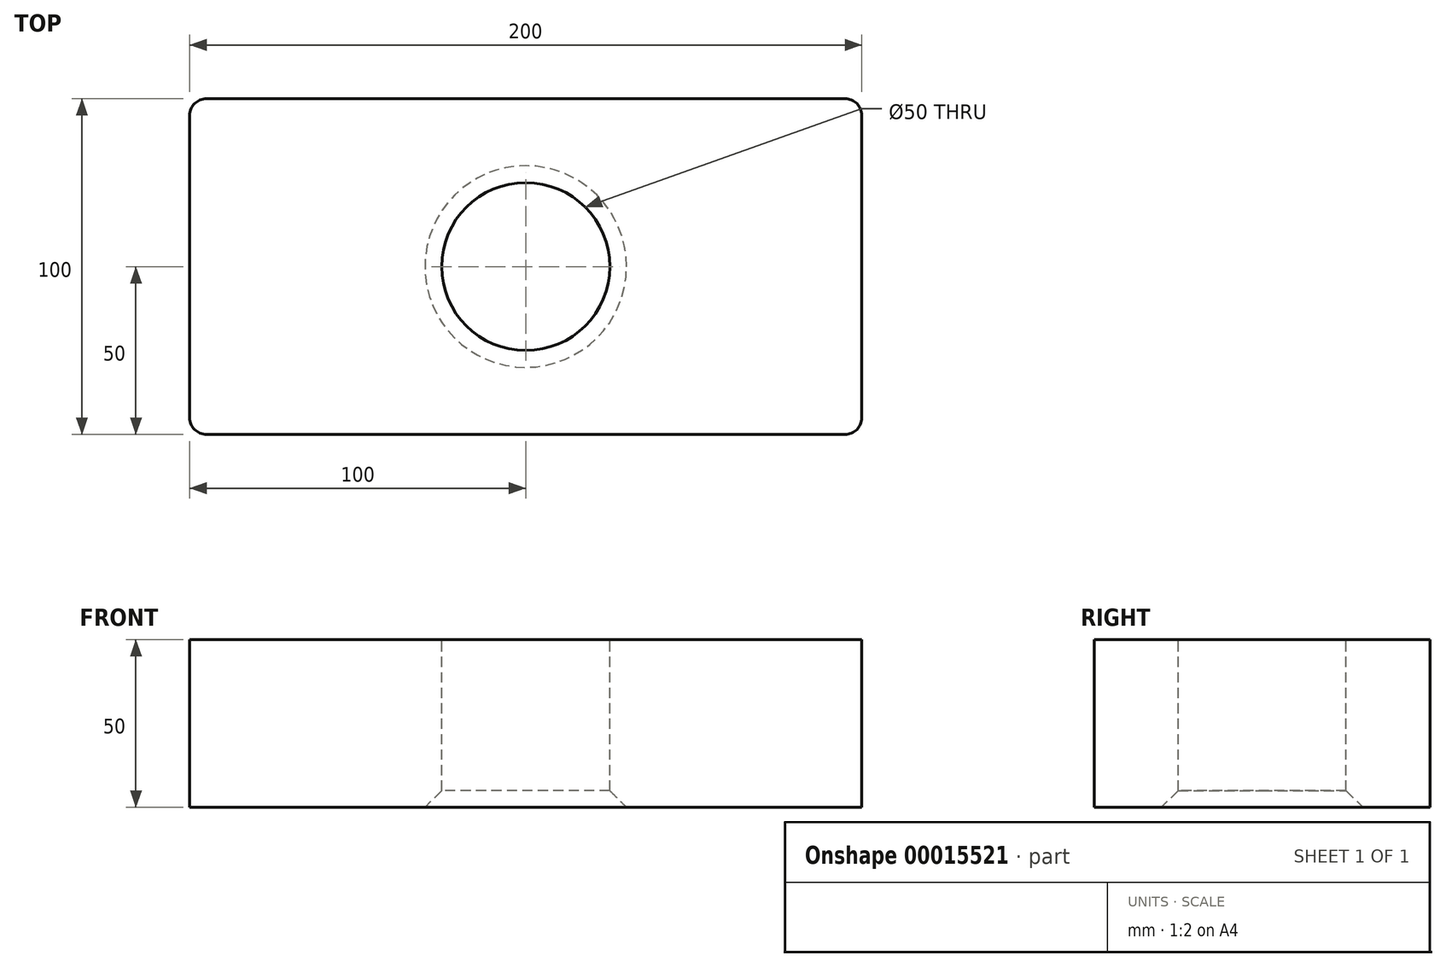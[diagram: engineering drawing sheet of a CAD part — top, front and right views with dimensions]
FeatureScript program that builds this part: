
annotation { "Feature Type Name" : "Feature", "Feature Type Description" : "" }
export const myFeature = defineFeature(function(context is Context, id is Id, definition is map)
    precondition{}
    {
        {
            var Q0;
            Q0=qCreatedBy(makeId("Top.planeOp"),FACE);
            var sketch = newSketch(context, id + "F0", { "sketchPlane" : qUnion([Q0])});
            skLineSegment(sketch, "E0.rect.bottom", {"start": v(100, 50) * mm, "end": v(-100, 50) * mm});
            skLineSegment(sketch, "E0.rect.top", {"start": v(100, -50) * mm, "end": v(-100, -50) * mm});
            skLineSegment(sketch, "E0.rect.left", {"start": v(100, 50) * mm, "end": v(100, -50) * mm});
            skLineSegment(sketch, "E0.rect.right", {"start": v(-100, 50) * mm, "end": v(-100, -50) * mm});
            skPoint(sketch, "E0.rect.middle", {"position": v(0, 0) * mm});
            skSolve(sketch);
        }
        {
            var Q0;
            Q0 = qSketchRegion(id + "F0", true);
            extrude(context, id + "F1", {"entities" : qUnion([Q0]), "depth" : 50 * mm});
        }
        {
            var Q0;
            Q0=makeQuery(id+"F1.opExtrude","SWEPT_EDGE",EDGE,{"disambiguationData":[OSD([sQuery(id+"F0.wireOp",EDGE,"E0.rect.top"),sQuery(id+"F0.wireOp",EDGE,"E0.rect.right")])]});
            var Q1;
            Q1=makeQuery(id+"F1.opExtrude","SWEPT_EDGE",EDGE,{"disambiguationData":[OSD([sQuery(id+"F0.wireOp",EDGE,"E0.rect.top"),sQuery(id+"F0.wireOp",EDGE,"E0.rect.left")])]});
            var Q2;
            Q2=makeQuery(id+"F1.opExtrude","SWEPT_EDGE",EDGE,{"disambiguationData":[OSD([sQuery(id+"F0.wireOp",EDGE,"E0.rect.bottom"),sQuery(id+"F0.wireOp",EDGE,"E0.rect.left")])]});
            var Q3;
            Q3=makeQuery(id+"F1.opExtrude","SWEPT_EDGE",EDGE,{"disambiguationData":[OSD([sQuery(id+"F0.wireOp",EDGE,"E0.rect.bottom"),sQuery(id+"F0.wireOp",EDGE,"E0.rect.right")])]});
            fillet(context, id + "F2", {"entities" : qUnion([Q0, Q1, Q2, Q3]), "radius" : 5 * mm, "tangentPropagation" : true, "allowEdgeOverflow" : false});
        }
        {
            var Q0;
            Q0=makeQuery(id+"F1.opExtrude","CAP_FACE",FACE,{"disambiguationData":[OSD([sQuery(id+"F0.wireOp",EDGE,"E0.rect.bottom"),sQuery(id+"F0.wireOp",EDGE,"E0.rect.top"),sQuery(id+"F0.wireOp",EDGE,"E0.rect.left"),sQuery(id+"F0.wireOp",EDGE,"E0.rect.right")])],"isStart":false});
            var sketch = newSketch(context, id + "F3", { "sketchPlane" : qUnion([Q0])});
            skCircle(sketch, "E1", {"center": v(0, 0) * mm, "radius": 25 * mm});
            skSolve(sketch);
        }
        {
            var Q0;
            Q0 = qSketchRegion(id + "F3", true);
            extrude(context, id + "F4", {"entities" : qUnion([Q0]), "operationType" : NewBodyOperationType.REMOVE, "endBound" : BoundingType.THROUGH_ALL, "oppositeDirection" : true, "depth" : 25 * mm});
        }
        {
            var Q0;
            Q0=makeQuery(id+"F4.boolean.opBoolean","COPY",EDGE,{"derivedFrom":makeQuery(id+"F4.opExtrude","CAP_EDGE",EDGE,{"disambiguationData":[OSD([sQuery(id+"F3.wireOp",EDGE,"E1")])],"isStart":true})});
            var Q1;
            Q1=makeQuery(id+"F4.boolean.opBoolean","INTERSECT",EDGE,{"derivedFrom":[makeQuery(id+"F1.opExtrude","CAP_FACE",FACE,{"disambiguationData":[OSD([sQuery(id+"F0.wireOp",EDGE,"E0.rect.bottom"),sQuery(id+"F0.wireOp",EDGE,"E0.rect.top"),sQuery(id+"F0.wireOp",EDGE,"E0.rect.left"),sQuery(id+"F0.wireOp",EDGE,"E0.rect.right")])],"isStart":true}),makeQuery(id+"F4.opExtrude","SWEPT_FACE",FACE,{"disambiguationData":[OSD([sQuery(id+"F3.wireOp",EDGE,"E1")])]})]});
            chamfer(context, id + "F5", {"entities" : qUnion([Q0, Q1]), "width" : 5 * mm, "tangentPropagation" : true});
        }
    });
